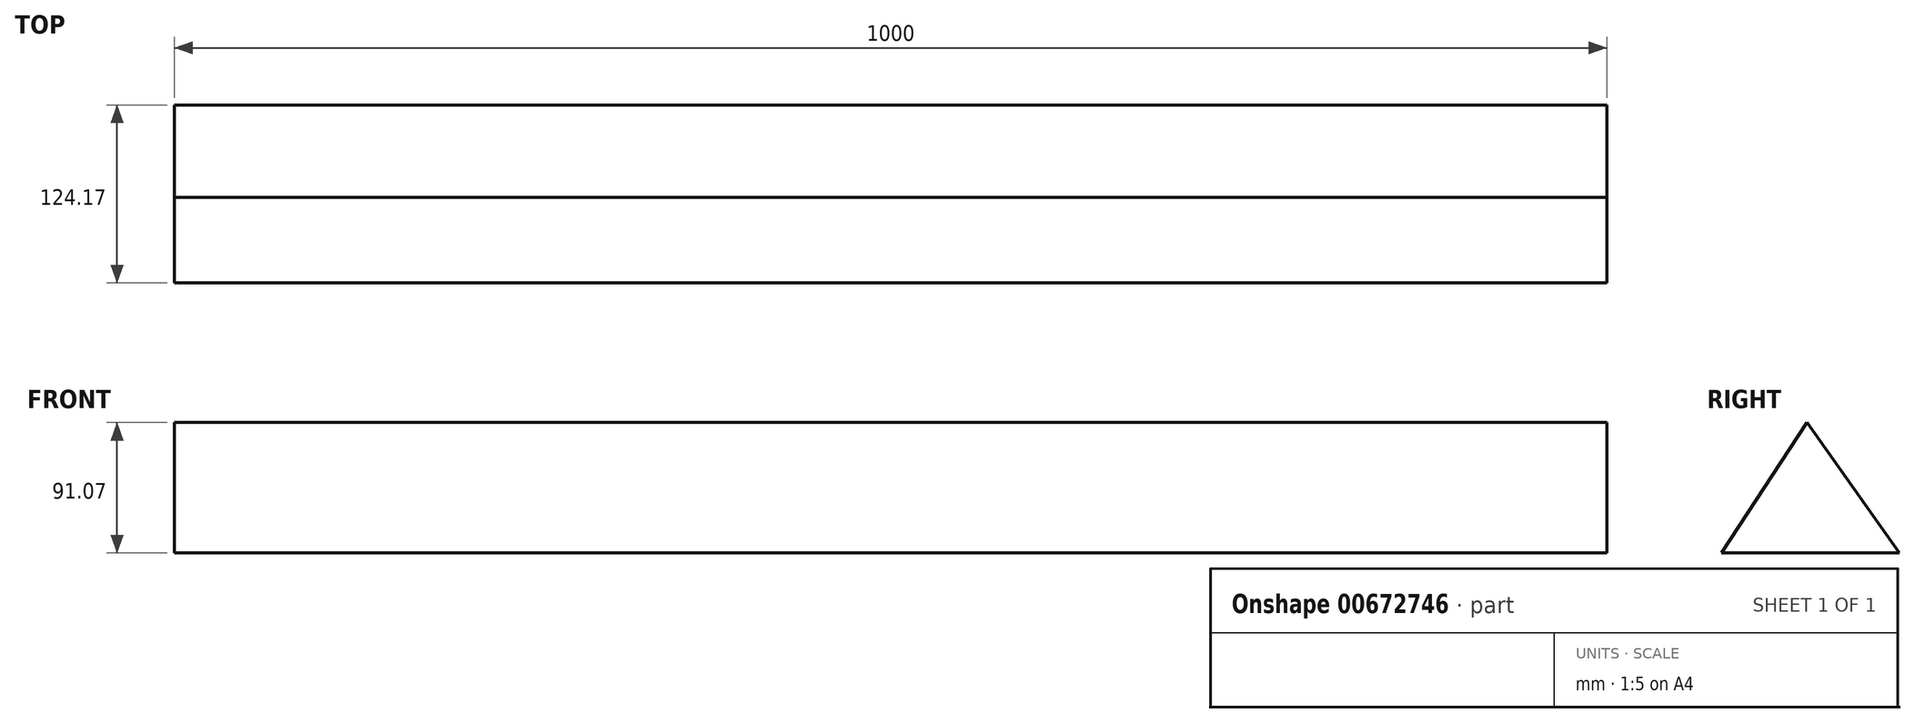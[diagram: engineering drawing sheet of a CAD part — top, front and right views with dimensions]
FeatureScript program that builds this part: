
annotation { "Feature Type Name" : "Feature", "Feature Type Description" : "" }
export const myFeature = defineFeature(function(context is Context, id is Id, definition is map)
    precondition{}
    {
        {
            var Q0;
            Q0=qCreatedBy(makeId("Right.planeOp"),FACE);
            var sketch = newSketch(context, id + "F0", { "sketchPlane" : qUnion([Q0])});
            skLineSegment(sketch, "E0", {"start": v(0, 91.07) * mm, "end": v(-59.87, 0) * mm});
            skLineSegment(sketch, "E1", {"start": v(-59.87, 0) * mm, "end": v(64.3, 0) * mm});
            skLineSegment(sketch, "E2", {"start": v(64.3, 0) * mm, "end": v(0, 91.07) * mm});
            skSolve(sketch);
        }
        {
            var Q0;
            Q0=makeQuery(id+"F0.imprint","IMPRINT",FACE,{"disambiguationData":[TD([[makeQuery(id+"F0.imprint","IMPRINT",EDGE,{"derivedFrom":sQuery(id+"F0.wireOp",EDGE,"E0")}),1.0]])]});
            extrude(context, id + "F1", {"entities" : qUnion([Q0]), "depth" : 1000 * mm, "offsetDistance" : 25.4 * mm});
        }
    });
